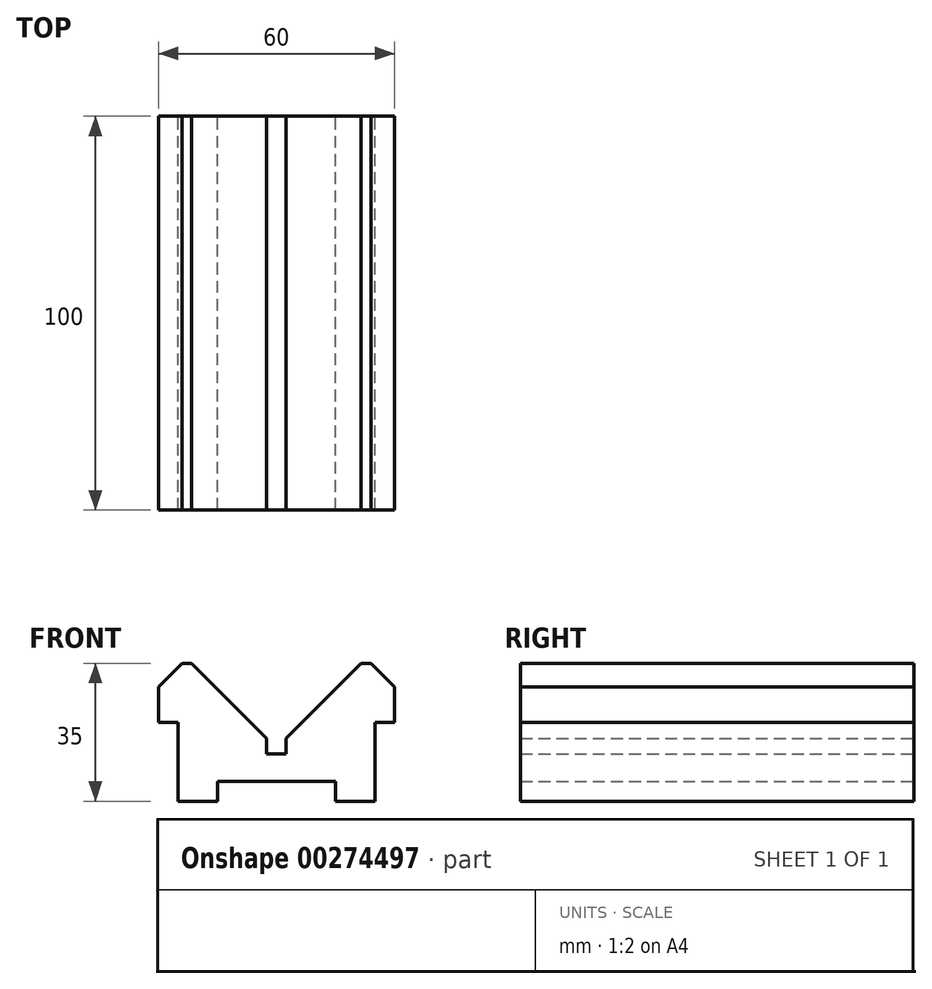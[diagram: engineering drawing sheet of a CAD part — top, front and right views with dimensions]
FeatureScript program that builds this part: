
annotation { "Feature Type Name" : "Feature", "Feature Type Description" : "" }
export const myFeature = defineFeature(function(context is Context, id is Id, definition is map)
    precondition{}
    {
        {
            var Q0;
            Q0=qCreatedBy(makeId("Front.planeOp"),FACE);
            var sketch = newSketch(context, id + "F0", { "sketchPlane" : qUnion([Q0])});
            skLineSegment(sketch, "E0.left", {"start": v(-30, 11.5) * mm, "end": v(-30, 2.5) * mm});
            skLineSegment(sketch, "E0.right", {"start": v(30, 11.5) * mm, "end": v(30, 2.5) * mm});
            skLineSegment(sketch, "E1.top", {"start": v(-30, 2.5) * mm, "end": v(-25, 2.5) * mm});
            skLineSegment(sketch, "E1.right", {"start": v(-25, -17.5) * mm, "end": v(-25, 2.5) * mm});
            skLineSegment(sketch, "E2.top", {"start": v(30, 2.5) * mm, "end": v(25, 2.5) * mm});
            skLineSegment(sketch, "E2.right", {"start": v(25, -17.5) * mm, "end": v(25, 2.5) * mm});
            skLineSegment(sketch, "E3", {"start": v(30, 11.5) * mm, "end": v(24, 17.5) * mm});
            skLineSegment(sketch, "E4", {"start": v(-30, 11.5) * mm, "end": v(-24, 17.5) * mm});
            skLineSegment(sketch, "E5.bottom", {"start": v(-15, -12.5) * mm, "end": v(15, -12.5) * mm});
            skLineSegment(sketch, "E5.left", {"start": v(-15, -12.5) * mm, "end": v(-15, -17.5) * mm});
            skLineSegment(sketch, "E5.right", {"start": v(15, -12.5) * mm, "end": v(15, -17.5) * mm});
            skLineSegment(sketch, "E6.trimOffspring", {"start": v(15, -17.5) * mm, "end": v(25, -17.5) * mm});
            skLineSegment(sketch, "E7", {"start": v(-25, -17.5) * mm, "end": v(-15, -17.5) * mm});
            skLineSegment(sketch, "E8.bottom", {"start": v(2.5, -5.5) * mm, "end": v(-2.5, -5.5) * mm});
            skLineSegment(sketch, "E8.left", {"start": v(2.5, -5.5) * mm, "end": v(2.5, -1.5) * mm});
            skLineSegment(sketch, "E8.right", {"start": v(-2.5, -5.5) * mm, "end": v(-2.5, -1.5) * mm});
            skLineSegment(sketch, "E9", {"start": v(-24, 17.5) * mm, "end": v(-21.5, 17.5) * mm});
            skLineSegment(sketch, "E10", {"start": v(21.5, 17.5) * mm, "end": v(24, 17.5) * mm});
            skPoint(sketch, "E11.orphan", {"position": v(21.5, 17.5) * mm});
            skLineSegment(sketch, "E12", {"start": v(2.5, -1.5) * mm, "end": v(21.5, 17.5) * mm});
            skPoint(sketch, "E13.bottom.end.orphan", {"position": v(2.5, 17.5) * mm});
            skLineSegment(sketch, "E14", {"start": v(-21.5, 17.5) * mm, "end": v(-2.5, -1.5) * mm});
            skSolve(sketch);
        }
        {
            var Q0;
            Q0=makeQuery(id+"F0.imprint","IMPRINT",FACE,{"disambiguationData":[TD([[makeQuery(id+"F0.imprint","IMPRINT",EDGE,{"derivedFrom":sQuery(id+"F0.wireOp",EDGE,"E0.left")}),1.0]])]});
            extrude(context, id + "F1", {"entities" : qUnion([Q0]), "depth" : 100 * mm});
        }
    });
